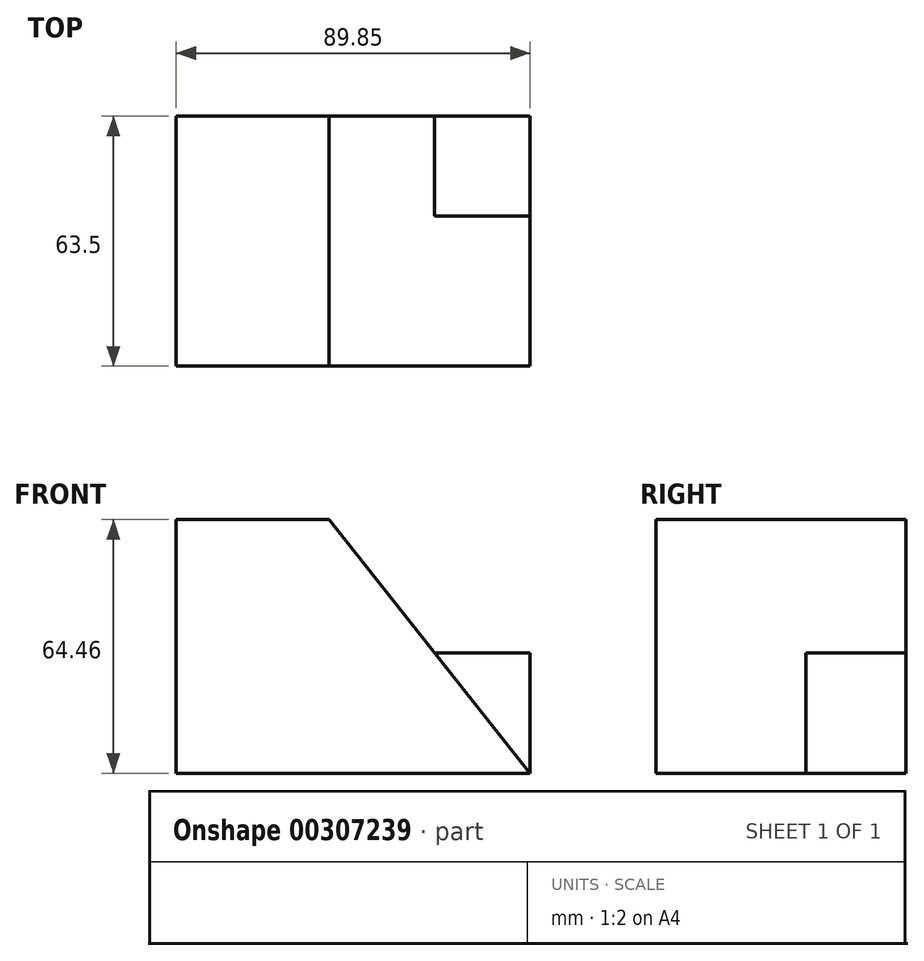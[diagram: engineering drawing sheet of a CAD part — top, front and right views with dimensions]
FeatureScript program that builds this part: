
annotation { "Feature Type Name" : "Feature", "Feature Type Description" : "" }
export const myFeature = defineFeature(function(context is Context, id is Id, definition is map)
    precondition{}
    {
        {
            var Q0;
            Q0=qCreatedBy(makeId("Front.planeOp"),FACE);
            var sketch = newSketch(context, id + "F0", { "sketchPlane" : qUnion([Q0])});
            skLineSegment(sketch, "E0", {"start": v(-63.9, 46.35) * mm, "end": v(-63.9, -18.11) * mm});
            skLineSegment(sketch, "E1", {"start": v(-63.9, -18.11) * mm, "end": v(25.96, -18.11) * mm});
            skLineSegment(sketch, "E2", {"start": v(-63.9, 46.35) * mm, "end": v(-25.1, 46.35) * mm});
            skLineSegment(sketch, "E3", {"start": v(-25.1, 46.35) * mm, "end": v(25.96, -18.11) * mm});
            skSolve(sketch);
        }
        {
            var Q0;
            Q0 = qSketchRegion(id + "F0", true);
            extrude(context, id + "F1", {"entities" : qUnion([Q0]), "depth" : 63.5 * mm});
        }
        {
            var Q0;
            Q0=makeQuery(id+"F1.opExtrude","CAP_FACE",FACE,{"disambiguationData":[OSD([sQuery(id+"F0.wireOp",EDGE,"E0"),sQuery(id+"F0.wireOp",EDGE,"E1"),sQuery(id+"F0.wireOp",EDGE,"E2"),sQuery(id+"F0.wireOp",EDGE,"E3")])],"isStart":true});
            var sketch = newSketch(context, id + "F2", { "sketchPlane" : qUnion([Q0])});
            skPoint(sketch, "E4.endSnap0", {"position": v(-0.43, 14.12) * mm});
            skLineSegment(sketch, "E5", {"start": v(-25.96, -18.11) * mm, "end": v(-25.96, 12.54) * mm});
            skLineSegment(sketch, "E6", {"start": v(-25.96, 12.54) * mm, "end": v(-1.68, 12.54) * mm});
            skLineSegment(sketch, "E7", {"start": v(-1.68, 12.54) * mm, "end": v(-25.96, -18.11) * mm});
            skSolve(sketch);
        }
        {
            var Q0;
            Q0 = qSketchRegion(id + "F2", true);
            extrude(context, id + "F3", {"entities" : qUnion([Q0]), "operationType" : NewBodyOperationType.ADD, "oppositeDirection" : true, "depth" : 25.4 * mm});
        }
    });
